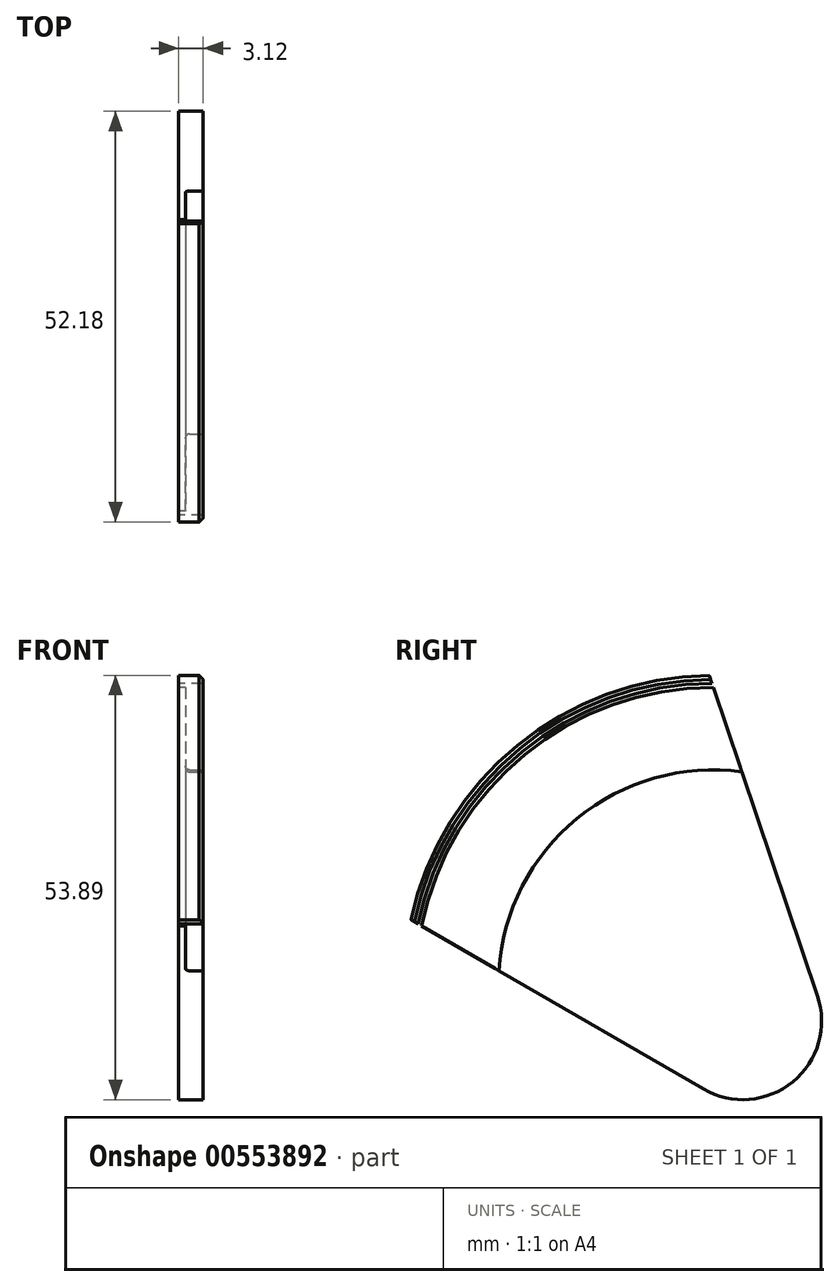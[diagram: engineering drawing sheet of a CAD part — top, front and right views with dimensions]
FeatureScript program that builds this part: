
annotation { "Feature Type Name" : "Feature", "Feature Type Description" : "" }
export const myFeature = defineFeature(function(context is Context, id is Id, definition is map)
    precondition{}
    {
        {
            var Q0;
            Q0=qCreatedBy(makeId("Right.planeOp"),FACE);
            var sketch = newSketch(context, id + "F0", { "sketchPlane" : qUnion([Q0])});
            skLineSegment(sketch, "E0", {"start": v(-70.5, 81.28) * mm, "end": v(-46.56, 52.03) * mm});
            skLineSegment(sketch, "E1", {"start": v(-46.56, 52.03) * mm, "end": v(-24.84, 25.5) * mm});
            skLineSegment(sketch, "E2", {"start": v(-46.56, 89.83) * mm, "end": v(-37.58, 63.21) * mm});
            skLineSegment(sketch, "E3", {"start": v(-83.62, 59.5) * mm, "end": v(-59.3, 45.43) * mm});
            skPoint(sketch, "E4.visualSharp", {"position": v(-24.84, 25.5) * mm});
            skArc(sketch, "E4.filletArc", {"start": v(-59.3, 45.43) * mm, "mid": v(-42.29, 46.8) * mm, "end": v(-37.58, 63.21) * mm});
            skArc(sketch, "E5", {"start": v(-46.56, 89.83) * mm, "mid": v(-70.5, 81.28) * mm, "end": v(-83.62, 59.5) * mm});
            skLineSegment(sketch, "E6", {"start": v(-24.84, 25.5) * mm, "end": v(0, 0) * mm});
            skSolve(sketch);
        }
        {
            var Q0;
            Q0=qSketchRegion(id+"F0",true);
            extrude(context, id + "F1", {"entities" : qUnion([Q0]), "depth" : 2.37 * mm, "offsetDistance" : 25 * mm});
        }
        {
            var Q0;
            Q0=makeQuery(id+"F1.opExtrude","CAP_FACE",FACE,{"disambiguationData":[OSD([sQuery(id+"F0.wireOp",EDGE,"E2"),sQuery(id+"F0.wireOp",EDGE,"E3"),sQuery(id+"F0.wireOp",EDGE,"E4.filletArc"),sQuery(id+"F0.wireOp",EDGE,"E5")])],"isStart":true});
            var sketch = newSketch(context, id + "F2", { "sketchPlane" : qUnion([Q0])});
            skArc(sketch, "E7.0", {"start": v(47.07, 91.33) * mm, "mid": v(71.45, 82.44) * mm, "end": v(84.98, 60.3) * mm});
            skArc(sketch, "E8.0", {"start": v(46.73, 90.33) * mm, "mid": v(70.82, 81.67) * mm, "end": v(84.07, 59.77) * mm});
            skLineSegment(sketch, "E9", {"start": v(37.58, 63.21) * mm, "end": v(47.07, 91.33) * mm});
            skLineSegment(sketch, "E10", {"start": v(59.3, 45.43) * mm, "end": v(84.98, 60.3) * mm});
            skArc(sketch, "E11.0", {"start": v(42.93, 79.09) * mm, "mid": v(63.85, 73.16) * mm, "end": v(73.8, 53.82) * mm});
            skArc(sketch, "E12.0", {"start": v(42.58, 78.03) * mm, "mid": v(63.22, 72.38) * mm, "end": v(72.83, 53.26) * mm});
            skSolve(sketch);
        }
        {
            var Q0;
            {var subQ0=sQuery(id+"F2.wireOp",EDGE,"E8.0");Q0=makeQuery(id+"F2.imprint","IMPRINT",FACE,{"disambiguationData":[TD([[makeQuery(id+"F2.imprint","IMPRINT",EDGE,{"derivedFrom":subQ0}),-1.0]])]});}
            var Q1;
            {var subQ0=sQuery(id+"F2.wireOp",EDGE,"E7.0");Q1=makeQuery(id+"F2.imprint","IMPRINT",FACE,{"disambiguationData":[TD([[makeQuery(id+"F2.imprint","IMPRINT",EDGE,{"derivedFrom":subQ0}),-1.0]])]});}
            extrude(context, id + "F3", {"entities" : qUnion([Q0, Q1]), "operationType" : NewBodyOperationType.ADD, "oppositeDirection" : true, "depth" : 2.37 * mm, "offsetDistance" : 25 * mm});
        }
        {
            var Q0;
            {var subQ0=sQuery(id+"F0.wireOp",EDGE,"E5");Q0=makeQuery(id+"F3.boolean.opBoolean","MERGE",FACE,{"derivedFrom":[makeQuery(id+"F1.opExtrude","CAP_FACE",FACE,{"disambiguationData":[OSD([sQuery(id+"F0.wireOp",EDGE,"E2"),sQuery(id+"F0.wireOp",EDGE,"E3"),sQuery(id+"F0.wireOp",EDGE,"E4.filletArc"),subQ0])],"isStart":false}),makeQuery(id+"F3.opExtrude","CAP_FACE",FACE,{"disambiguationData":[OSD([subQ0,sQuery(id+"F2.wireOp",EDGE,"E7.0"),sQuery(id+"F2.wireOp",EDGE,"E9"),sQuery(id+"F2.wireOp",EDGE,"E10")])],"isStart":false})]});}
            var sketch = newSketch(context, id + "F4", { "sketchPlane" : qUnion([Q0])});
            skArc(sketch, "E13.0", {"start": v(-42.93, 79.09) * mm, "mid": v(-63.85, 73.16) * mm, "end": v(-73.8, 53.82) * mm});
            skArc(sketch, "E14.converted", {"start": v(-46.73, 90.33) * mm, "mid": v(-70.82, 81.67) * mm, "end": v(-84.07, 59.77) * mm});
            skLineSegment(sketch, "E15", {"start": v(-73.8, 53.82) * mm, "end": v(-84.07, 59.77) * mm});
            skSolve(sketch);
        }
        {
            var Q0;
            {var subQ0=sQuery(id+"F4.wireOp",EDGE,"E13.0");Q0=makeQuery(id+"F4.imprint","IMPRINT",FACE,{"disambiguationData":[TD([[makeQuery(id+"F4.imprint","IMPRINT",EDGE,{"derivedFrom":subQ0}),-1.0]])]});}
            extrude(context, id + "F5", {"entities" : qUnion([Q0]), "operationType" : NewBodyOperationType.REMOVE, "oppositeDirection" : true, "depth" : 2.25 * mm, "offsetDistance" : 25 * mm});
        }
        {
            var Q0;
            {var subQ0=sQuery(id+"F0.wireOp",EDGE,"E5");Q0=makeQuery(id+"F3.boolean.opBoolean","MERGE",FACE,{"derivedFrom":[makeQuery(id+"F1.opExtrude","CAP_FACE",FACE,{"disambiguationData":[OSD([sQuery(id+"F0.wireOp",EDGE,"E2"),sQuery(id+"F0.wireOp",EDGE,"E3"),sQuery(id+"F0.wireOp",EDGE,"E4.filletArc"),subQ0])],"isStart":true}),makeQuery(id+"F3.opExtrude","CAP_FACE",FACE,{"disambiguationData":[OSD([subQ0,sQuery(id+"F2.wireOp",EDGE,"E7.0"),sQuery(id+"F2.wireOp",EDGE,"E9"),sQuery(id+"F2.wireOp",EDGE,"E10")])],"isStart":true})]});}
            extrude(context, id + "F6", {"entities" : qUnion([Q0]), "operationType" : NewBodyOperationType.ADD, "depth" : .75 * mm, "offsetDistance" : 25 * mm});
        }
        {
            var Q0;
            Q0=makeQuery(id+"F3.opExtrude","CAP_EDGE",EDGE,{"disambiguationData":[OSD([sQuery(id+"F2.wireOp",EDGE,"E7.0")])],"isStart":false});
            var Q1;
            Q1=makeQuery(id+"F5.boolean.opBoolean","COPY",EDGE,{"derivedFrom":makeQuery(id+"F5.opExtrude","CAP_EDGE",EDGE,{"disambiguationData":[OSD([sQuery(id+"F4.wireOp",EDGE,"E13.0")])],"isStart":true})});
            chamfer(context, id + "F7", {"entities" : qUnion([Q0, Q1]), "width" : .5 * mm, "tangentPropagation" : true});
        }
        {
            var Q0;
            Q0=makeQuery(id+"F5.boolean.opBoolean","COPY",EDGE,{"derivedFrom":makeQuery(id+"F5.opExtrude","CAP_EDGE",EDGE,{"disambiguationData":[OSD([sQuery(id+"F4.wireOp",EDGE,"E14.converted")])],"isStart":false})});
            var Q1;
            Q1=makeQuery(id+"F5.boolean.opBoolean","COPY",EDGE,{"derivedFrom":makeQuery(id+"F5.opExtrude","CAP_EDGE",EDGE,{"disambiguationData":[OSD([sQuery(id+"F4.wireOp",EDGE,"E13.0")])],"isStart":false})});
            fillet(context, id + "F8", {"entities" : qUnion([Q0, Q1]), "radius" : .5 * mm, "tangentPropagation" : true, "allowEdgeOverflow" : false});
        }
        {
            var Q0;
            Q0=makeQuery(id+"F6.opExtrude","CAP_FACE",FACE,{"disambiguationData":[OSD([sQuery(id+"F0.wireOp",EDGE,"E2"),sQuery(id+"F0.wireOp",EDGE,"E3"),sQuery(id+"F0.wireOp",EDGE,"E4.filletArc"),sQuery(id+"F0.wireOp",EDGE,"E5"),sQuery(id+"F2.wireOp",EDGE,"E7.0"),sQuery(id+"F2.wireOp",EDGE,"E9"),sQuery(id+"F2.wireOp",EDGE,"E10")])],"isStart":false});
            var sketch = newSketch(context, id + "F9", { "sketchPlane" : qUnion([Q0])});
            skLineSegment(sketch, "E16", {"start": v(47.07, 91.33) * mm, "end": v(33.33, 50.64) * mm});
            skLineSegment(sketch, "E17", {"start": v(84.98, 60.3) * mm, "end": v(47.81, 38.78) * mm});
            skArc(sketch, "E18.filletArc", {"start": v(33.33, 50.64) * mm, "mid": v(36.47, 39.7) * mm, "end": v(47.81, 38.78) * mm});
            skSolve(sketch);
        }
        {
            var Q0;
            {var subQ2=sQuery(id+"F9.wireOp",EDGE,"E18.filletArc");Q0=makeQuery(id+"F9.imprint","IMPRINT",FACE,{"disambiguationData":[TD([[makeQuery(id+"F9.imprint","IMPRINT",EDGE,{"derivedFrom":subQ2}),1.0]])]});}
            extrude(context, id + "F10", {"entities" : qUnion([Q0]), "operationType" : NewBodyOperationType.ADD, "oppositeDirection" : true, "depth" : 3.12 * mm, "offsetDistance" : 25 * mm});
        }
    });
